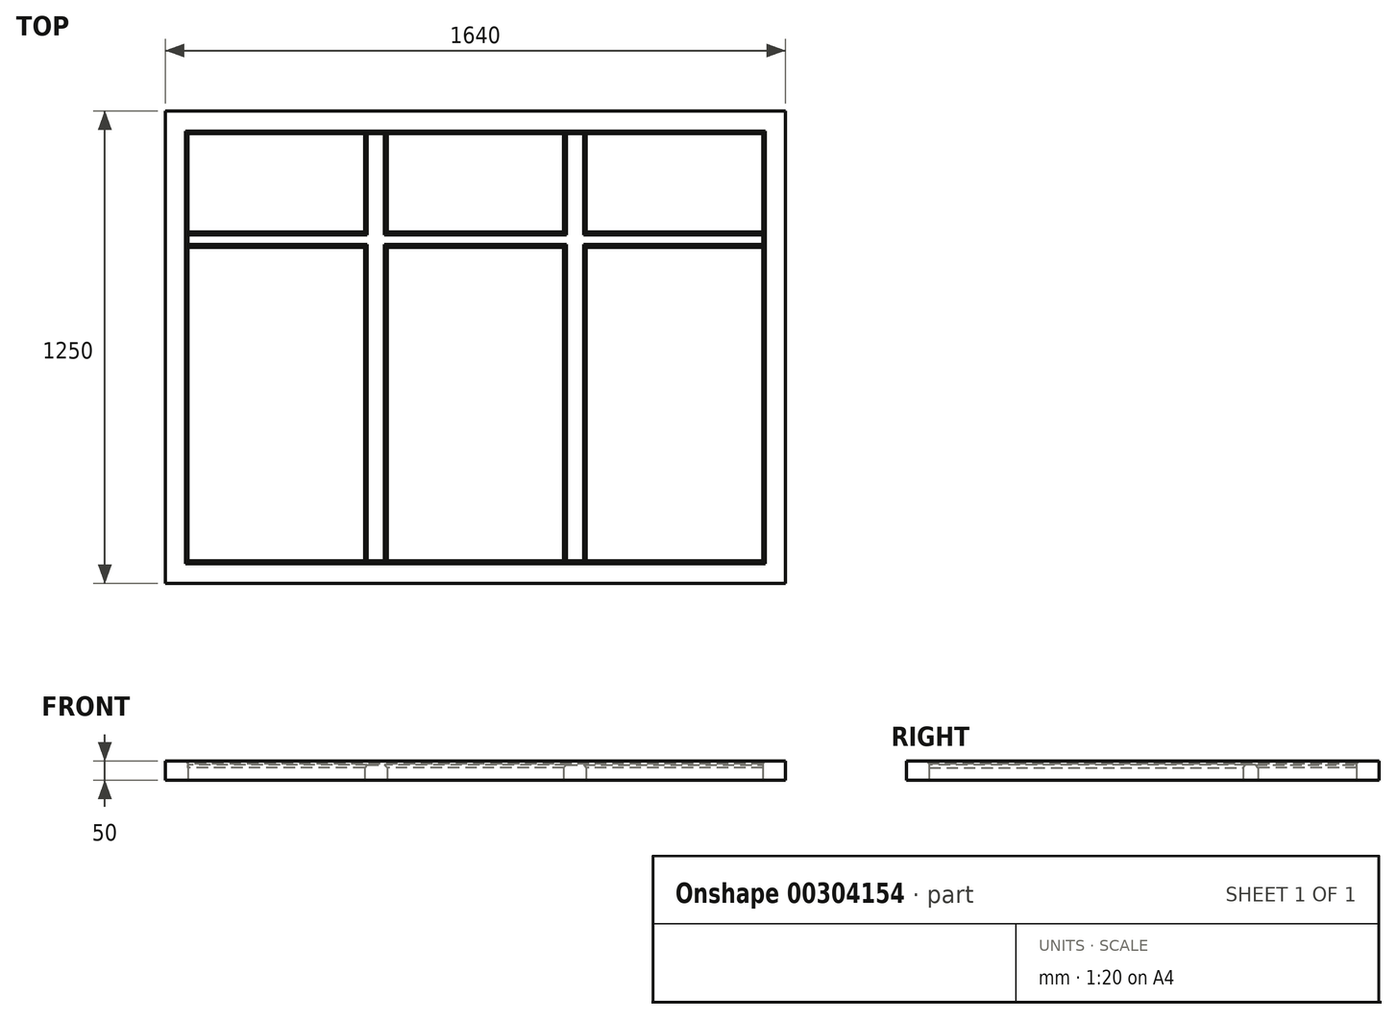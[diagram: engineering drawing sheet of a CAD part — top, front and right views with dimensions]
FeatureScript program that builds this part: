
annotation { "Feature Type Name" : "Feature", "Feature Type Description" : "" }
export const myFeature = defineFeature(function(context is Context, id is Id, definition is map)
    precondition{}
    {
        {
            var Q0;
            Q0=qCreatedBy(makeId("Top.planeOp"),FACE);
            var sketch = newSketch(context, id + "F0", { "sketchPlane" : qUnion([Q0])});
            skLineSegment(sketch, "E0.bottom", {"start": v(-317.02, 715.2) * mm, "end": v(1322.98, 715.2) * mm});
            skLineSegment(sketch, "E0.top", {"start": v(-317.02, -534.8) * mm, "end": v(1322.98, -534.8) * mm});
            skLineSegment(sketch, "E0.left", {"start": v(-317.02, 715.2) * mm, "end": v(-317.02, -534.8) * mm});
            skLineSegment(sketch, "E0.right", {"start": v(1322.98, 715.2) * mm, "end": v(1322.98, -534.8) * mm});
            skLineSegment(sketch, "E1.bottom", {"start": v(-257.02, 655.2) * mm, "end": v(209.65, 655.2) * mm});
            skLineSegment(sketch, "E1.top", {"start": v(-257.02, 395.2) * mm, "end": v(209.65, 395.2) * mm});
            skLineSegment(sketch, "E1.left", {"start": v(-257.02, 655.2) * mm, "end": v(-257.02, 395.2) * mm});
            skLineSegment(sketch, "E1.right", {"start": v(209.65, 655.2) * mm, "end": v(209.65, 395.2) * mm});
            skLineSegment(sketch, "E2.bottom", {"start": v(269.65, 655.2) * mm, "end": v(736.31, 655.2) * mm});
            skLineSegment(sketch, "E2.top", {"start": v(269.65, 395.2) * mm, "end": v(736.31, 395.2) * mm});
            skLineSegment(sketch, "E2.left", {"start": v(269.65, 655.2) * mm, "end": v(269.65, 395.2) * mm});
            skLineSegment(sketch, "E2.right", {"start": v(736.31, 655.2) * mm, "end": v(736.31, 395.2) * mm});
            skLineSegment(sketch, "E3.bottom", {"start": v(-257.02, 355.2) * mm, "end": v(209.65, 355.2) * mm});
            skLineSegment(sketch, "E3.top", {"start": v(-257.02, -474.8) * mm, "end": v(209.65, -474.8) * mm});
            skLineSegment(sketch, "E3.left", {"start": v(-257.02, 355.2) * mm, "end": v(-257.02, -474.8) * mm});
            skLineSegment(sketch, "E3.right", {"start": v(209.65, 355.2) * mm, "end": v(209.65, -474.8) * mm});
            skLineSegment(sketch, "E4.bottom", {"start": v(269.65, 355.2) * mm, "end": v(736.31, 355.2) * mm});
            skLineSegment(sketch, "E4.top", {"start": v(269.65, -474.8) * mm, "end": v(736.31, -474.8) * mm});
            skLineSegment(sketch, "E4.left", {"start": v(269.65, 355.2) * mm, "end": v(269.65, -474.8) * mm});
            skLineSegment(sketch, "E4.right", {"start": v(736.31, 355.2) * mm, "end": v(736.31, -474.8) * mm});
            skLineSegment(sketch, "E5.bottom", {"start": v(796.31, 355.2) * mm, "end": v(1262.98, 355.2) * mm});
            skLineSegment(sketch, "E5.top", {"start": v(796.31, -474.8) * mm, "end": v(1262.98, -474.8) * mm});
            skLineSegment(sketch, "E5.left", {"start": v(796.31, 355.2) * mm, "end": v(796.31, -474.8) * mm});
            skLineSegment(sketch, "E5.right", {"start": v(1262.98, 355.2) * mm, "end": v(1262.98, -474.8) * mm});
            skLineSegment(sketch, "E6.bottom", {"start": v(796.31, 655.2) * mm, "end": v(1262.98, 655.2) * mm});
            skLineSegment(sketch, "E6.top", {"start": v(796.31, 395.2) * mm, "end": v(1262.98, 395.2) * mm});
            skLineSegment(sketch, "E6.left", {"start": v(796.31, 655.2) * mm, "end": v(796.31, 395.2) * mm});
            skLineSegment(sketch, "E6.right", {"start": v(1262.98, 655.2) * mm, "end": v(1262.98, 395.2) * mm});
            skLineSegment(sketch, "E7", {"start": v(-257.02, 395.2) * mm, "end": v(-257.02, 355.2) * mm});
            skLineSegment(sketch, "E8", {"start": v(209.65, -474.8) * mm, "end": v(269.65, -474.8) * mm});
            skLineSegment(sketch, "E9", {"start": v(736.31, -474.8) * mm, "end": v(796.31, -474.8) * mm});
            skLineSegment(sketch, "E10", {"start": v(1262.98, 355.2) * mm, "end": v(1262.98, 395.2) * mm});
            skLineSegment(sketch, "E11", {"start": v(796.31, 655.2) * mm, "end": v(736.31, 655.2) * mm});
            skLineSegment(sketch, "E12", {"start": v(269.65, 655.2) * mm, "end": v(209.65, 655.2) * mm});
            skSolve(sketch);
        }
        {
            var Q0;
            Q0=makeQuery(id+"F0.imprint","IMPRINT",FACE,{"disambiguationData":[TD([[makeQuery(id+"F0.imprint","IMPRINT",EDGE,{"derivedFrom":sQuery(id+"F0.wireOp",EDGE,"E0.bottom")}),-1.0]])]});
            extrude(context, id + "F1", {"entities" : qUnion([Q0]), "depth" : 50 * mm});
        }
        {
            var Q0;
            Q0=makeQuery(id+"F0.imprint","IMPRINT",FACE,{"disambiguationData":[TD([[makeQuery(id+"F0.imprint","IMPRINT",EDGE,{"derivedFrom":sQuery(id+"F0.wireOp",EDGE,"E1.top")}),-1.0]])]});
            extrude(context, id + "F2", {"entities" : qUnion([Q0]), "depth" : 40 * mm, "offsetDistance" : 25 * mm});
        }
        {
            var Q0;
            Q0=makeQuery(id+"F1.opExtrude","CAP_EDGE",EDGE,{"disambiguationData":[OSD([sQuery(id+"F0.wireOp",EDGE,"ytPpMPqZ-kEHr-QmaY-d1DR-AzYH62YFSOlj.left")])],"isStart":false});
            var Q1;
            Q1=makeQuery(id+"F1.opExtrude","CAP_EDGE",EDGE,{"disambiguationData":[OSD([sQuery(id+"F0.wireOp",EDGE,"ytPpMPqZ-kEHr-QmaY-d1DR-AzYH62YFSOlj.bottom")])],"isStart":false});
            var Q2;
            Q2=makeQuery(id+"F1.opExtrude","CAP_EDGE",EDGE,{"disambiguationData":[OSD([sQuery(id+"F0.wireOp",EDGE,"ytPpMPqZ-kEHr-QmaY-d1DR-AzYH62YFSOlj.right")])],"isStart":false});
            var Q3;
            Q3=makeQuery(id+"F1.opExtrude","CAP_EDGE",EDGE,{"disambiguationData":[OSD([sQuery(id+"F0.wireOp",EDGE,"ytPpMPqZ-kEHr-QmaY-d1DR-AzYH62YFSOlj.top")])],"isStart":false});
            var Q4;
            Q4=makeQuery(id+"F1.opExtrude","CAP_EDGE",EDGE,{"disambiguationData":[OSD([sQuery(id+"F0.wireOp",EDGE,"r7QiBjje-UKbf-qYST-CBBd-TYCSkPhiPhca.top")])],"isStart":false});
            var Q5;
            Q5=makeQuery(id+"F1.opExtrude","CAP_EDGE",EDGE,{"disambiguationData":[OSD([sQuery(id+"F0.wireOp",EDGE,"r7QiBjje-UKbf-qYST-CBBd-TYCSkPhiPhca.bottom")])],"isStart":false});
            var Q6;
            Q6=makeQuery(id+"F1.opExtrude","CAP_EDGE",EDGE,{"disambiguationData":[OSD([sQuery(id+"F0.wireOp",EDGE,"r7QiBjje-UKbf-qYST-CBBd-TYCSkPhiPhca.left")])],"isStart":false});
            var Q7;
            Q7=makeQuery(id+"F1.opExtrude","CAP_EDGE",EDGE,{"disambiguationData":[OSD([sQuery(id+"F0.wireOp",EDGE,"r7QiBjje-UKbf-qYST-CBBd-TYCSkPhiPhca.right")])],"isStart":false});
            var Q8;
            Q8=makeQuery(id+"F1.opExtrude","CAP_EDGE",EDGE,{"disambiguationData":[OSD([sQuery(id+"F0.wireOp",EDGE,"HfWFaPNu-mQyP-ler6-jSu7-HC3u6uNNGoQA.left")])],"isStart":false});
            var Q9;
            Q9=makeQuery(id+"F1.opExtrude","CAP_EDGE",EDGE,{"disambiguationData":[OSD([sQuery(id+"F0.wireOp",EDGE,"HfWFaPNu-mQyP-ler6-jSu7-HC3u6uNNGoQA.bottom")])],"isStart":false});
            var Q10;
            Q10=makeQuery(id+"F1.opExtrude","CAP_EDGE",EDGE,{"disambiguationData":[OSD([sQuery(id+"F0.wireOp",EDGE,"HfWFaPNu-mQyP-ler6-jSu7-HC3u6uNNGoQA.right")])],"isStart":false});
            var Q11;
            Q11=makeQuery(id+"F1.opExtrude","CAP_EDGE",EDGE,{"disambiguationData":[OSD([sQuery(id+"F0.wireOp",EDGE,"HfWFaPNu-mQyP-ler6-jSu7-HC3u6uNNGoQA.top")])],"isStart":false});
            var Q12;
            Q12=makeQuery(id+"F1.opExtrude","CAP_EDGE",EDGE,{"disambiguationData":[OSD([sQuery(id+"F0.wireOp",EDGE,"5wbdZzbv-KT36-aS9W-tHdP-7188U3jB6Ytn.bottom")])],"isStart":false});
            var Q13;
            Q13=makeQuery(id+"F1.opExtrude","CAP_EDGE",EDGE,{"disambiguationData":[OSD([sQuery(id+"F0.wireOp",EDGE,"5wbdZzbv-KT36-aS9W-tHdP-7188U3jB6Ytn.left")])],"isStart":false});
            var Q14;
            Q14=makeQuery(id+"F1.opExtrude","CAP_EDGE",EDGE,{"disambiguationData":[OSD([sQuery(id+"F0.wireOp",EDGE,"5wbdZzbv-KT36-aS9W-tHdP-7188U3jB6Ytn.top")])],"isStart":false});
            var Q15;
            Q15=makeQuery(id+"F1.opExtrude","CAP_EDGE",EDGE,{"disambiguationData":[OSD([sQuery(id+"F0.wireOp",EDGE,"5wbdZzbv-KT36-aS9W-tHdP-7188U3jB6Ytn.right")])],"isStart":false});
            var Q16;
            Q16=makeQuery(id+"F1.opExtrude","CAP_EDGE",EDGE,{"disambiguationData":[OSD([sQuery(id+"F0.wireOp",EDGE,"DTlHMEbU-aPmp-yZgJ-OWsR-Co97d6l2honQ.bottom")])],"isStart":false});
            var Q17;
            Q17=makeQuery(id+"F1.opExtrude","CAP_EDGE",EDGE,{"disambiguationData":[OSD([sQuery(id+"F0.wireOp",EDGE,"DTlHMEbU-aPmp-yZgJ-OWsR-Co97d6l2honQ.right")])],"isStart":false});
            var Q18;
            Q18=makeQuery(id+"F1.opExtrude","CAP_EDGE",EDGE,{"disambiguationData":[OSD([sQuery(id+"F0.wireOp",EDGE,"DTlHMEbU-aPmp-yZgJ-OWsR-Co97d6l2honQ.top")])],"isStart":false});
            var Q19;
            Q19=makeQuery(id+"F1.opExtrude","CAP_EDGE",EDGE,{"disambiguationData":[OSD([sQuery(id+"F0.wireOp",EDGE,"DTlHMEbU-aPmp-yZgJ-OWsR-Co97d6l2honQ.left")])],"isStart":false});
            var Q20;
            Q20=makeQuery(id+"F1.opExtrude","CAP_EDGE",EDGE,{"disambiguationData":[OSD([sQuery(id+"F0.wireOp",EDGE,"KnIwFXTZ-7AYv-IQ4P-MqQU-q16PSDZZjzCm.right")])],"isStart":false});
            var Q21;
            Q21=makeQuery(id+"F1.opExtrude","CAP_EDGE",EDGE,{"disambiguationData":[OSD([sQuery(id+"F0.wireOp",EDGE,"KnIwFXTZ-7AYv-IQ4P-MqQU-q16PSDZZjzCm.bottom")])],"isStart":false});
            var Q22;
            Q22=makeQuery(id+"F1.opExtrude","CAP_EDGE",EDGE,{"disambiguationData":[OSD([sQuery(id+"F0.wireOp",EDGE,"KnIwFXTZ-7AYv-IQ4P-MqQU-q16PSDZZjzCm.left")])],"isStart":false});
            var Q23;
            Q23=makeQuery(id+"F1.opExtrude","CAP_EDGE",EDGE,{"disambiguationData":[OSD([sQuery(id+"F0.wireOp",EDGE,"KnIwFXTZ-7AYv-IQ4P-MqQU-q16PSDZZjzCm.top")])],"isStart":false});
            var Q24;
            Q24=makeQuery(id+"F1.opExtrude","CAP_EDGE",EDGE,{"disambiguationData":[OSD([sQuery(id+"F0.wireOp",EDGE,"E1.left")])],"isStart":false});
            var Q25;
            Q25=makeQuery(id+"F1.opExtrude","CAP_EDGE",EDGE,{"disambiguationData":[OSD([sQuery(id+"F0.wireOp",EDGE,"E1.bottom")])],"isStart":false});
            var Q26;
            Q26=makeQuery(id+"F1.opExtrude","CAP_EDGE",EDGE,{"disambiguationData":[OSD([sQuery(id+"F0.wireOp",EDGE,"E1.right")])],"isStart":false});
            var Q27;
            Q27=makeQuery(id+"F1.opExtrude","CAP_EDGE",EDGE,{"disambiguationData":[OSD([sQuery(id+"F0.wireOp",EDGE,"2C36mqMa-A4eQ-qRDU-Ah7K-ji7NIf0B9ti7.left")])],"isStart":false});
            var Q28;
            Q28=makeQuery(id+"F1.opExtrude","CAP_EDGE",EDGE,{"disambiguationData":[OSD([sQuery(id+"F0.wireOp",EDGE,"2C36mqMa-A4eQ-qRDU-Ah7K-ji7NIf0B9ti7.bottom")])],"isStart":false});
            var Q29;
            Q29=makeQuery(id+"F1.opExtrude","CAP_EDGE",EDGE,{"disambiguationData":[OSD([sQuery(id+"F0.wireOp",EDGE,"2C36mqMa-A4eQ-qRDU-Ah7K-ji7NIf0B9ti7.right")])],"isStart":false});
            var Q30;
            Q30=makeQuery(id+"F1.opExtrude","CAP_EDGE",EDGE,{"disambiguationData":[OSD([sQuery(id+"F0.wireOp",EDGE,"E2.left")])],"isStart":false});
            var Q31;
            Q31=makeQuery(id+"F1.opExtrude","CAP_EDGE",EDGE,{"disambiguationData":[OSD([sQuery(id+"F0.wireOp",EDGE,"E2.bottom")])],"isStart":false});
            var Q32;
            Q32=makeQuery(id+"F1.opExtrude","CAP_EDGE",EDGE,{"disambiguationData":[OSD([sQuery(id+"F0.wireOp",EDGE,"E5.left")])],"isStart":false});
            var Q33;
            Q33=makeQuery(id+"F1.opExtrude","CAP_EDGE",EDGE,{"disambiguationData":[OSD([sQuery(id+"F0.wireOp",EDGE,"E5.bottom")])],"isStart":false});
            var Q34;
            Q34=makeQuery(id+"F1.opExtrude","CAP_EDGE",EDGE,{"disambiguationData":[OSD([sQuery(id+"F0.wireOp",EDGE,"E4.bottom")])],"isStart":false});
            var Q35;
            Q35=makeQuery(id+"F1.opExtrude","CAP_EDGE",EDGE,{"disambiguationData":[OSD([sQuery(id+"F0.wireOp",EDGE,"E4.left")])],"isStart":false});
            var Q36;
            Q36=makeQuery(id+"F1.opExtrude","CAP_EDGE",EDGE,{"disambiguationData":[OSD([sQuery(id+"F0.wireOp",EDGE,"E3.right")])],"isStart":false});
            var Q37;
            Q37=makeQuery(id+"F1.opExtrude","CAP_EDGE",EDGE,{"disambiguationData":[OSD([sQuery(id+"F0.wireOp",EDGE,"E3.bottom")])],"isStart":false});
            var Q38;
            Q38=makeQuery(id+"F1.opExtrude","CAP_EDGE",EDGE,{"disambiguationData":[OSD([sQuery(id+"F0.wireOp",EDGE,"E3.left")])],"isStart":false});
            var Q39;
            Q39=makeQuery(id+"F1.opExtrude","CAP_EDGE",EDGE,{"disambiguationData":[OSD([sQuery(id+"F0.wireOp",EDGE,"E2.right")])],"isStart":false});
            var Q40;
            Q40=makeQuery(id+"F1.opExtrude","CAP_EDGE",EDGE,{"disambiguationData":[OSD([sQuery(id+"F0.wireOp",EDGE,"E5.right")])],"isStart":false});
            var Q41;
            Q41=makeQuery(id+"F1.opExtrude","CAP_EDGE",EDGE,{"disambiguationData":[OSD([sQuery(id+"F0.wireOp",EDGE,"E2.top")])],"isStart":false});
            var Q42;
            Q42=makeQuery(id+"F1.opExtrude","CAP_EDGE",EDGE,{"disambiguationData":[OSD([sQuery(id+"F0.wireOp",EDGE,"2C36mqMa-A4eQ-qRDU-Ah7K-ji7NIf0B9ti7.top")])],"isStart":false});
            var Q43;
            Q43=makeQuery(id+"F1.opExtrude","CAP_EDGE",EDGE,{"disambiguationData":[OSD([sQuery(id+"F0.wireOp",EDGE,"E1.top")])],"isStart":false});
            var Q44;
            Q44=makeQuery(id+"F1.opExtrude","CAP_EDGE",EDGE,{"disambiguationData":[OSD([sQuery(id+"F0.wireOp",EDGE,"E4.top")])],"isStart":false});
            var Q45;
            Q45=makeQuery(id+"F1.opExtrude","CAP_EDGE",EDGE,{"disambiguationData":[OSD([sQuery(id+"F0.wireOp",EDGE,"E5.top")])],"isStart":false});
            var Q46;
            Q46=makeQuery(id+"F1.opExtrude","CAP_EDGE",EDGE,{"disambiguationData":[OSD([sQuery(id+"F0.wireOp",EDGE,"E3.top")])],"isStart":false});
            var Q47;
            Q47=makeQuery(id+"F1.opExtrude","CAP_EDGE",EDGE,{"disambiguationData":[OSD([sQuery(id+"F0.wireOp",EDGE,"E6.left")])],"isStart":false});
            var Q48;
            Q48=makeQuery(id+"F1.opExtrude","CAP_EDGE",EDGE,{"disambiguationData":[OSD([sQuery(id+"F0.wireOp",EDGE,"E6.bottom")])],"isStart":false});
            var Q49;
            Q49=makeQuery(id+"F1.opExtrude","CAP_EDGE",EDGE,{"disambiguationData":[OSD([sQuery(id+"F0.wireOp",EDGE,"E6.right")])],"isStart":false});
            var Q50;
            Q50=makeQuery(id+"F1.opExtrude","CAP_EDGE",EDGE,{"disambiguationData":[OSD([sQuery(id+"F0.wireOp",EDGE,"E6.top")])],"isStart":false});
            var Q51;
            Q51=makeQuery(id+"F2.opExtrude","CAP_EDGE",EDGE,{"disambiguationData":[OSD([sQuery(id+"F0.wireOp",EDGE,"E3.bottom")])],"isStart":false});
            var Q52;
            Q52=makeQuery(id+"F2.opExtrude","CAP_EDGE",EDGE,{"disambiguationData":[OSD([sQuery(id+"F0.wireOp",EDGE,"E4.bottom")])],"isStart":false});
            var Q53;
            Q53=makeQuery(id+"F2.opExtrude","CAP_EDGE",EDGE,{"disambiguationData":[OSD([sQuery(id+"F0.wireOp",EDGE,"E4.left")])],"isStart":false});
            var Q54;
            Q54=makeQuery(id+"F2.opExtrude","CAP_EDGE",EDGE,{"disambiguationData":[OSD([sQuery(id+"F0.wireOp",EDGE,"E5.left")])],"isStart":false});
            var Q55;
            Q55=makeQuery(id+"F2.opExtrude","CAP_EDGE",EDGE,{"disambiguationData":[OSD([sQuery(id+"F0.wireOp",EDGE,"E6.left")])],"isStart":false});
            var Q56;
            Q56=makeQuery(id+"F2.opExtrude","CAP_EDGE",EDGE,{"disambiguationData":[OSD([sQuery(id+"F0.wireOp",EDGE,"E2.left")])],"isStart":false});
            var Q57;
            Q57=makeQuery(id+"F2.opExtrude","CAP_EDGE",EDGE,{"disambiguationData":[OSD([sQuery(id+"F0.wireOp",EDGE,"E3.right")])],"isStart":false});
            var Q58;
            Q58=makeQuery(id+"F2.opExtrude","CAP_EDGE",EDGE,{"disambiguationData":[OSD([sQuery(id+"F0.wireOp",EDGE,"E1.right")])],"isStart":false});
            var Q59;
            Q59=makeQuery(id+"F2.opExtrude","CAP_EDGE",EDGE,{"disambiguationData":[OSD([sQuery(id+"F0.wireOp",EDGE,"E1.top")])],"isStart":false});
            var Q60;
            Q60=makeQuery(id+"F2.opExtrude","CAP_EDGE",EDGE,{"disambiguationData":[OSD([sQuery(id+"F0.wireOp",EDGE,"E2.top")])],"isStart":false});
            var Q61;
            Q61=makeQuery(id+"F2.opExtrude","CAP_EDGE",EDGE,{"disambiguationData":[OSD([sQuery(id+"F0.wireOp",EDGE,"E6.top")])],"isStart":false});
            var Q62;
            Q62=makeQuery(id+"F2.opExtrude","CAP_EDGE",EDGE,{"disambiguationData":[OSD([sQuery(id+"F0.wireOp",EDGE,"E5.bottom")])],"isStart":false});
            var Q63;
            Q63=makeQuery(id+"F2.opExtrude","CAP_EDGE",EDGE,{"disambiguationData":[OSD([sQuery(id+"F0.wireOp",EDGE,"E4.right")])],"isStart":false});
            var Q64;
            Q64=makeQuery(id+"F2.opExtrude","CAP_EDGE",EDGE,{"disambiguationData":[OSD([sQuery(id+"F0.wireOp",EDGE,"E2.right")])],"isStart":false});
            chamfer(context, id + "F3", {"entities" : qUnion([Q0, Q1, Q2, Q3, Q4, Q5, Q6, Q7, Q8, Q9, Q10, Q11, Q12, Q13, Q14, Q15, Q16, Q17, Q18, Q19, Q20, Q21, Q22, Q23, Q24, Q25, Q26, Q27, Q28, Q29, Q30, Q31, Q32, Q33, Q34, Q35, Q36, Q37, Q38, Q39, Q40, Q41, Q42, Q43, Q44, Q45, Q46, Q47, Q48, Q49, Q50, Q51, Q52, Q53, Q54, Q55, Q56, Q57, Q58, Q59, Q60, Q61, Q62, Q63, Q64]), "width" : 7 * mm, "tangentPropagation" : true});
        }
    });
